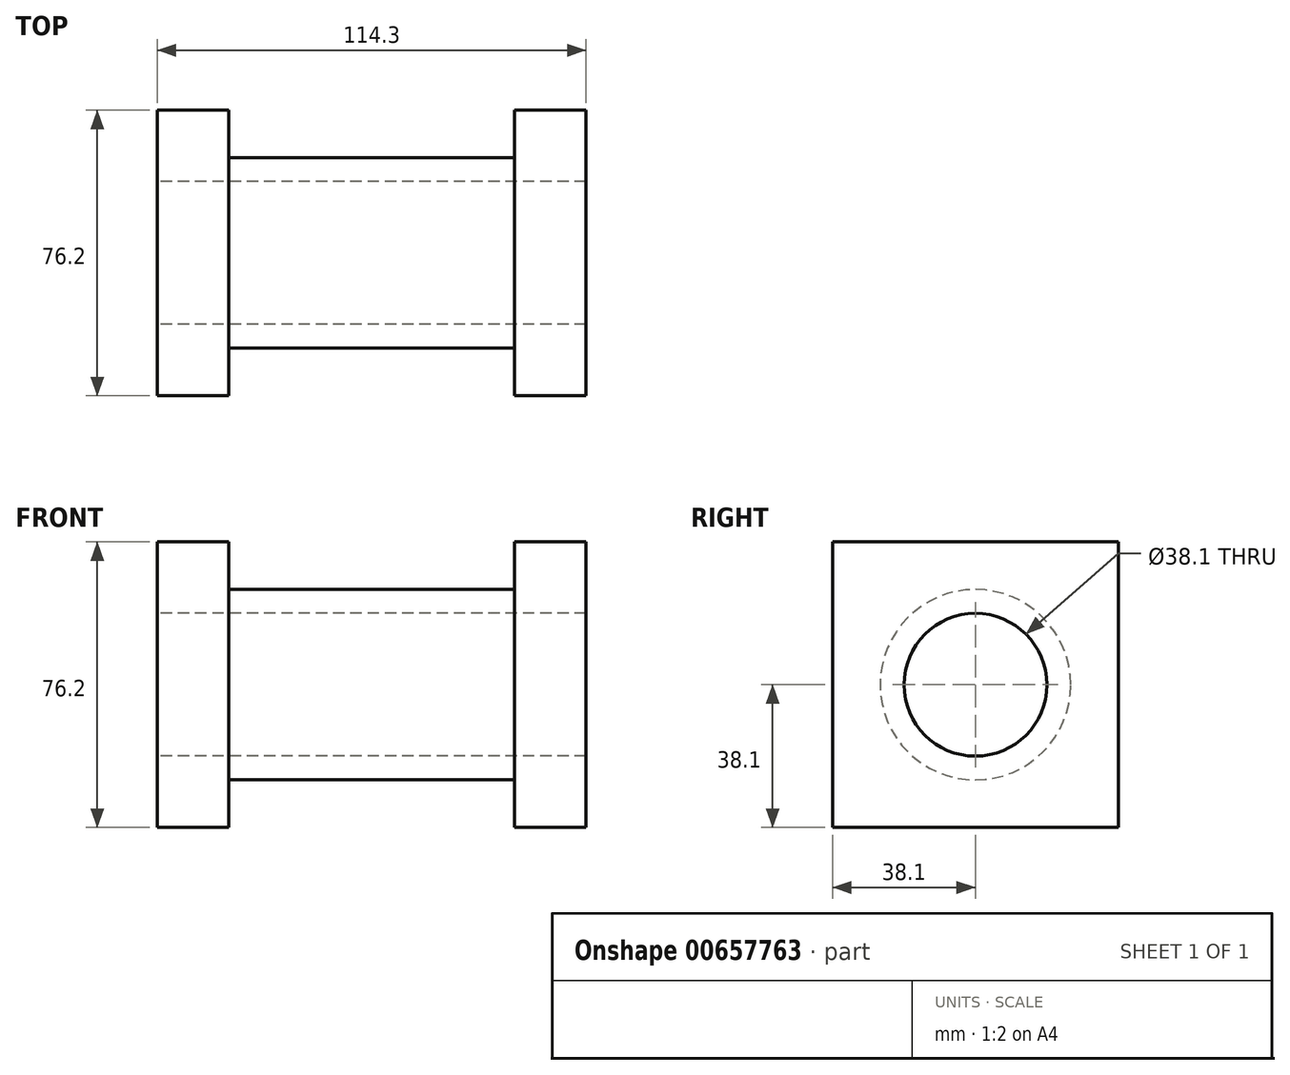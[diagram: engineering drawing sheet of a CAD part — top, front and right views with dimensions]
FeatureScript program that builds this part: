
annotation { "Feature Type Name" : "Feature", "Feature Type Description" : "" }
export const myFeature = defineFeature(function(context is Context, id is Id, definition is map)
    precondition{}
    {
        {
            var Q0;
            Q0=qCreatedBy(makeId("Right.planeOp"),FACE);
            var sketch = newSketch(context, id + "F0", { "sketchPlane" : qUnion([Q0])});
            skLineSegment(sketch, "E0.bottom", {"start": v(38.1, 38.1) * mm, "end": v(-38.1, 38.1) * mm});
            skLineSegment(sketch, "E0.top", {"start": v(38.1, -38.1) * mm, "end": v(-38.1, -38.1) * mm});
            skLineSegment(sketch, "E0.left", {"start": v(38.1, 38.1) * mm, "end": v(38.1, -38.1) * mm});
            skLineSegment(sketch, "E0.right", {"start": v(-38.1, 38.1) * mm, "end": v(-38.1, -38.1) * mm});
            skPoint(sketch, "E0.middle", {"position": v(0, 0) * mm});
            skSolve(sketch);
        }
        {
            var Q0;
            Q0=makeQuery(id+"F0.imprint","IMPRINT",FACE,{"disambiguationData":[TD([[makeQuery(id+"F0.imprint","IMPRINT",EDGE,{"derivedFrom":sQuery(id+"F0.wireOp",EDGE,"E0.bottom")}),1.0]])]});
            extrude(context, id + "F1", {"entities" : qUnion([Q0]), "depth" : 19.05 * mm, "offsetDistance" : 25.4 * mm});
        }
        {
            var Q0;
            Q0=makeQuery(id+"F1.opExtrude","CAP_FACE",FACE,{"disambiguationData":[OSD([sQuery(id+"F0.wireOp",EDGE,"E0.bottom"),sQuery(id+"F0.wireOp",EDGE,"E0.top"),sQuery(id+"F0.wireOp",EDGE,"E0.left"),sQuery(id+"F0.wireOp",EDGE,"E0.right")])],"isStart":false});
            var sketch = newSketch(context, id + "F2", { "sketchPlane" : qUnion([Q0])});
            skCircle(sketch, "E1", {"center": v(0, 0) * mm, "radius": 25.4 * mm});
            skSolve(sketch);
        }
        {
            var Q0;
            Q0=makeQuery(id+"F2.imprint","IMPRINT",FACE,{"disambiguationData":[TD([[makeQuery(id+"F2.imprint","IMPRINT",EDGE,{"derivedFrom":sQuery(id+"F2.wireOp",EDGE,"E1")}),1.0]])]});
            extrude(context, id + "F3", {"entities" : qUnion([Q0]), "operationType" : NewBodyOperationType.ADD, "depth" : 76.2 * mm, "offsetDistance" : 25.4 * mm});
        }
        {
            var Q0;
            Q0=makeQuery(id+"F3.opExtrude","CAP_FACE",FACE,{"disambiguationData":[OSD([sQuery(id+"F2.wireOp",EDGE,"E1")])],"isStart":false});
            var sketch = newSketch(context, id + "F4", { "sketchPlane" : qUnion([Q0])});
            skLineSegment(sketch, "E2.bottom", {"start": v(38.1, 38.1) * mm, "end": v(-38.1, 38.1) * mm});
            skLineSegment(sketch, "E2.top", {"start": v(38.1, -38.1) * mm, "end": v(-38.1, -38.1) * mm});
            skLineSegment(sketch, "E2.left", {"start": v(38.1, 38.1) * mm, "end": v(38.1, -38.1) * mm});
            skLineSegment(sketch, "E2.right", {"start": v(-38.1, 38.1) * mm, "end": v(-38.1, -38.1) * mm});
            skPoint(sketch, "E2.middle", {"position": v(0, 0) * mm});
            skSolve(sketch);
        }
        {
            var Q0;
            Q0=makeQuery(id+"F4.imprint","IMPRINT",FACE,{"disambiguationData":[TD([[makeQuery(id+"F4.imprint","IMPRINT",EDGE,{"derivedFrom":sQuery(id+"F4.wireOp",EDGE,"E2.bottom")}),1.0]])]});
            var Q1;
            Q1=makeQuery(id+"F4.imprint","IMPRINT",FACE,{"disambiguationData":[TD([[makeQuery(id+"F4.imprint","IMPRINT",EDGE,{"derivedFrom":makeQuery(id+"F3.opExtrude","CAP_EDGE",EDGE,{"disambiguationData":[OSD([sQuery(id+"F2.wireOp",EDGE,"E1")])],"isStart":false})}),1.0]])]});
            extrude(context, id + "F5", {"entities" : qUnion([Q0, Q1]), "operationType" : NewBodyOperationType.ADD, "depth" : 19.05 * mm, "offsetDistance" : 25.4 * mm});
        }
        {
            var Q0;
            Q0=makeQuery(id+"F1.opExtrude","CAP_FACE",FACE,{"disambiguationData":[OSD([sQuery(id+"F0.wireOp",EDGE,"E0.bottom"),sQuery(id+"F0.wireOp",EDGE,"E0.top"),sQuery(id+"F0.wireOp",EDGE,"E0.left"),sQuery(id+"F0.wireOp",EDGE,"E0.right")])],"isStart":true});
            var sketch = newSketch(context, id + "F6", { "sketchPlane" : qUnion([Q0])});
            skCircle(sketch, "E3", {"center": v(0, 0) * mm, "radius": 19.05 * mm});
            skSolve(sketch);
        }
        {
            var Q0;
            Q0=makeQuery(id+"F6.imprint","IMPRINT",FACE,{"disambiguationData":[TD([[makeQuery(id+"F6.imprint","IMPRINT",EDGE,{"derivedFrom":sQuery(id+"F6.wireOp",EDGE,"E3")}),1.0]])]});
            extrude(context, id + "F7", {"entities" : qUnion([Q0]), "operationType" : NewBodyOperationType.REMOVE, "oppositeDirection" : true, "depth" : 114.3 * mm, "offsetDistance" : 25.4 * mm});
        }
    });
